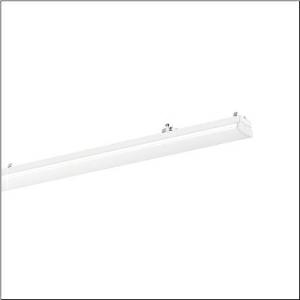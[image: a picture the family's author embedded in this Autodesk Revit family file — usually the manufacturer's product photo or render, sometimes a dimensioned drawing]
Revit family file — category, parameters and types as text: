
# Revit family: licross_21_recessed_opal_mo_52tl1ddn495g
name_source: partatom
category: Lighting Fixtures
units: mm (PartAtom-declared; Revit-internal decimal feet)

## family parameters
Cut with Voids When Loaded = No
Host = Face
Light Source = No
Part Type = Normal
Room Calculation Point = No
Round Connector Dimension = Use Diameter
Shared = No

## types (1)
- --- (1 x LED, 9740 lm, 58 W, 4000K)
    Apparent Load = 58 VA
    CIE Flux Codes = 44 73 91 87 100
    Color Rendering = 80
    Color Temperature = 4000K
    Default Elevation = 1800 mm
    Description = Licross 21 recessed opal MO, luminaire insert, of sheet steel, galvanised, coil coated, white, length: 1.500mm, width: 66mm, height: 67mm, LED rated luminous flux: 9.750lm, light colour: 840, SDCM (Standard Deviation of Colour Matching)MacAdam ≤ 3 SDCM (initial), control gear: DALI 2, with plug, 5-pole, with phase selection, mains connection: 220..240V, AC, 50/60Hz, rated input power: 58W, internal wiring halogen-free, primary optical cover: cover, of PMMA, light emission: direct with ceiling illumination distribution, primary light characteristic: symmetric, protection rating (complete): IP40, insulation class (complete): insulation class I (protective earthing), certification: CE, ENEC, VDE, UKCA, protection symbol: D if used in an environment without relevant dust loads with corresponding accessories, impact resistance: IK06, permissible ambient temperature for indoor applications: -25..+35°C, corresponds to IFS (International Featured Standards) requirements for safety and quality in the food industry, reducing of maximum allowable ambient temperature of 5°C with ceiling mounting, LABS conformity tested according to VDMA 24364:2018-05, The light source and the operating device comply with the requirements of the Ecodesign Regulation (EU) 2019/2020 and are replaceable in accordance with this regulation, packaging unit: 1 piece
    Height = 83 mm
    Lamp = 1 x LED
    Lamp Light Flux = 9740 lm
    Lamp Power = 58 W
    Lamp count = 1
    Length = 1500 mm
    Luminous efficacy = 168 lm/W
    Manufacturer = Siteco
    ModVariant = No
    Model = 52TL1DDN495G
    Mounting Place = Ceiling
    Mounting Type = Pendant
    Number of Poles = 1
    OnlyDefault = Yes
    Power Factor = 1
    Product Name = Licross 21 recessed opal MO
    Product group = luminaire insert | ceiling pendant
    ProductGroupID = 901
    Protection Class = Protection class I
    Protection Degree = IP 40
    RLX_Detail_Level = 1
    RLX_Emergency_Light_Flux = 0 lm
    RLX_Emergency_Type = 0
    RLX_Emergency_Type_DB = No
    RlxData = <blob elided: 27185 chars, md5=a2f748c9>
    Socket = socket
    Standby Power = 0 W
    System Light Flux = 9740 lm
    System Power = 58 W
    Type Comments = factory setting: luminous flux: 100 % | dim-lin: 254 | 390 mA
    Type Image = l_1313666.jpg
    URL = http://relux.com
    VarID = @adj_076329
    Voltage = 0 V
    Weight = 0.00 kg
    Width = 76 mm

## geometry (parser evidence)
native form markers: Blend x4, Sweep x12
no freeform markers — native parametric forms only
